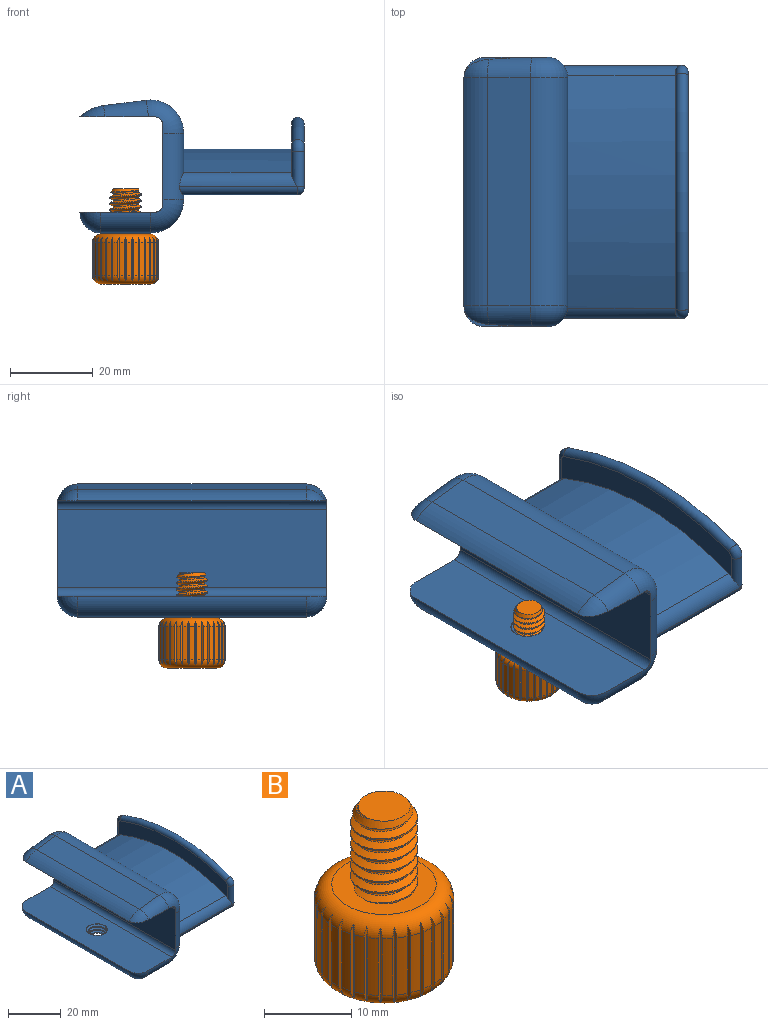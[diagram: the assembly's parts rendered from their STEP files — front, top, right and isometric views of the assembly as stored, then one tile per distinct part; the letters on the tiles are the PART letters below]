
ASSEMBLY  parts=2 mates=1
PART A: 48 faces, bbox 55x65.4x35.4 mm
  f0: plane 55x12mm, normal (0,0,-1), area 596.4mm2, adj f11,f21,f27,f45,f47
  f1: plane 55x7.37mm, normal (1,0,0), area 299.3mm2, adj f11,f12,f19,f25
  f2: cylinder r=71.97mm len=56.12mm, axis (-1,0,0), area 1498.9mm2, adj f3,f14,f19,f25,f28,f29
  f3: plane 55x9.15mm, normal (1,0,0), area 301.4mm2, adj f2,f4,f19,f25
  f4: cylinder r=8mm len=55mm, axis (0,1,0), area 745.8mm2, adj f3,f5,f18,f24
  f5: plane 55x10.32mm, normal (-0.12,0,0.99), area 572.1mm2, adj f4,f15,f17,f23
  f6: plane 65.07x18.25mm, normal (0,0,-1), area 1145.5mm2, adj f7,f15,f16,f17,f18,f22,f23,f24
  f7: cylinder r=2mm len=64.93mm, axis (0,1,0), area 203.7mm2, adj f6,f8,f18,f24
  f8: plane 65.32x19.32mm, normal (-1,0,0), area 1235mm2, adj f7,f9,f18,f19,f20,f24,f25,f26
  f9: cylinder r=2mm len=64.99mm, axis (0,1,0), area 204.2mm2, adj f8,f10,f20,f26
  f10: plane 65.43x18.43mm, normal (0,0,1), area 1112.2mm2, adj f9,f20,f21,f26,f27,f40,f41,f42
  f11: cylinder r=8mm len=55mm, axis (0,1,0), area 691.2mm2, adj f0,f1,f20,f26
  f12: cylinder r=66.97mm len=55.35mm, axis (-1,0,0), area 1569.1mm2, adj f1,f19,f25,f30,f31,f39
  f13: plane 58x15.66mm, normal (1,0,0), area 565.9mm2, adj f32,f33,f34,f35,f36,f37,f38,f39
  f14: plane 58x12.26mm, normal (-1,0,0), area 357.1mm2, adj f2,f28,f29,f32,f33,f34,f35,f36
  f15: cylinder r=10mm len=55mm, axis (0,-1,0), area 352.5mm2, adj f5,f6,f16,f22
  f16: torus R=5mm, axis (0,-1,0), area 25.3mm2, adj f6,f15,f17
  f17: cylinder r=5mm len=10.82mm, axis (-0.99,0,-0.12), area 64.4mm2, adj f5,f6,f16,f18
  f18: torus R=3mm, axis (0,-1,0), area 77.8mm2, adj f4,f6,f7,f8,f17,f19
  f19: cylinder r=5mm len=16.06mm, axis (0,0,1), area 112.4mm2, adj f1,f2,f3,f8,f12,f18,f20,f29
  f20: torus R=3mm, axis (0,-1,0), area 75.2mm2, adj f8,f9,f10,f11,f19,f21
  f21: cylinder r=5mm len=12mm, axis (1,0,0), area 94.2mm2, adj f0,f10,f20,f44
  f22: torus R=5mm, axis (0,-1,0), area 25.3mm2, adj f6,f15,f23
  f23: cylinder r=5mm len=10.82mm, axis (0.99,0,0.12), area 64.4mm2, adj f5,f6,f22,f24
  f24: torus R=3mm, axis (0,-1,0), area 77.8mm2, adj f4,f6,f7,f8,f23,f25
  f25: cylinder r=5mm len=16.06mm, axis (0,0,-1), area 112.4mm2, adj f1,f2,f3,f8,f12,f24,f26,f28
  f26: torus R=3mm, axis (0,-1,0), area 75.2mm2, adj f8,f9,f10,f11,f25,f27
  f27: cylinder r=5mm len=12mm, axis (-1,0,0), area 94.2mm2, adj f0,f10,f26,f46
  f28: cylinder r=4mm len=28.5mm, axis (-1,0,0), area 122.8mm2, adj f2,f14,f25,f30,f36,f38
  f29: cylinder r=4mm len=28.5mm, axis (-1,0,0), area 122.8mm2, adj f2,f14,f19,f31,f35,f37
  f30: cylinder r=2mm len=28.5mm, axis (-1,0,0), area 109.3mm2, adj f12,f25,f28,f38
  f31: cylinder r=2mm len=28.5mm, axis (-1,0,0), area 109.3mm2, adj f12,f19,f29,f37
  f32: torus R=77.97mm, axis (1,0,0), area 273.6mm2, adj f13,f14,f33,f34
  f33: torus R=1.5mm, axis (1,0,0), area 13.9mm2, adj f13,f14,f32,f35
  f34: torus R=1.5mm, axis (1,0,0), area 13.9mm2, adj f13,f14,f32,f36
  f35: cylinder r=1.5mm len=8.55mm, axis (0,0,-1), area 37mm2, adj f13,f14,f29,f33,f37
  f36: cylinder r=1.5mm len=8.55mm, axis (0,0,1), area 37mm2, adj f13,f14,f28,f34,f38
  f37: torus R=0.5mm, axis (1,0,0), area 6.9mm2, adj f13,f29,f31,f35,f39
  f38: torus R=0.5mm, axis (1,0,0), area 6.9mm2, adj f13,f28,f30,f36,f39
  f39: torus R=68.47mm, axis (1,0,0), area 135.5mm2, adj f12,f13,f37,f38
  f40: bspline ~9.96x8.62mm, area 67.9mm2, adj f10,f42,f43,f47
  f41: bspline ~9.96x8.62mm, area 68mm2, adj f10,f42,f43,f47
  f42: bspline ~10.12x8.76mm, area 19mm2, adj f10,f40,f41,f47
  f43: cylinder r=3.5mm len=7mm, axis (0,0,1), area 22mm2, adj f10,f40,f41,f47
  f44: sphere r=5mm, area 39.3mm2, adj f10,f21,f45
  f45: cylinder r=5mm len=55mm, axis (0,-1,0), area 432mm2, adj f0,f10,f44,f46
  f46: sphere r=5mm, area 39.3mm2, adj f10,f27,f45
  f47: cone r=4.5mm half-angle=45deg, axis (0,0,-1), area 23.4mm2, adj f0,f40,f41,f42,f43
PART B: 100 faces, bbox 17.7x17.7x23.9 mm
  f0: cylinder r=3.85mm len=9.53mm, axis (0,0,1), area 21.6mm2, adj f2,f3,f37,f99
  f1: bspline ~12.13x7.02mm, area 57.8mm2, adj f2,f3,f37,f38,f99
  f2: bspline ~11.72x8.89mm, area 138.5mm2, adj f0,f1,f37,f99
  f3: bspline ~12.22x8.89mm, area 138.1mm2, adj f0,f1,f37,f99
  f4: cylinder r=8mm len=8mm, axis (0,0,1), area 9.7mm2, adj f33,f34,f96,f97
  f5: cylinder r=8mm len=8mm, axis (0,0,1), area 9.7mm2, adj f33,f34,f94,f95
  f6: cylinder r=8mm len=8mm, axis (0,0,1), area 9.7mm2, adj f33,f34,f92,f93
  f7: cylinder r=8mm len=8mm, axis (0,0,1), area 9.7mm2, adj f33,f34,f90,f91
  f8: cylinder r=8mm len=8mm, axis (0,0,1), area 9.7mm2, adj f33,f34,f88,f89
  f9: cylinder r=8mm len=8mm, axis (0,0,1), area 9.7mm2, adj f33,f34,f86,f87
  f10: cylinder r=8mm len=8mm, axis (0,0,1), area 9.7mm2, adj f33,f34,f84,f85
  f11: cylinder r=8mm len=8mm, axis (0,0,1), area 9.7mm2, adj f33,f34,f82,f83
  f12: cylinder r=8mm len=8mm, axis (0,0,1), area 9.7mm2, adj f33,f34,f80,f81
  f13: cylinder r=8mm len=8mm, axis (0,0,1), area 9.7mm2, adj f33,f34,f78,f79
  f14: cylinder r=8mm len=8mm, axis (0,0,1), area 9.7mm2, adj f33,f34,f76,f77
  f15: cylinder r=8mm len=8mm, axis (0,0,1), area 9.7mm2, adj f33,f34,f74,f75
  f16: cylinder r=8mm len=8mm, axis (0,0,1), area 9.7mm2, adj f33,f34,f72,f73
  f17: cylinder r=8mm len=8mm, axis (0,0,1), area 9.7mm2, adj f33,f34,f70,f71
  f18: cylinder r=8mm len=8mm, axis (0,0,1), area 9.7mm2, adj f33,f34,f68,f69
  f19: cylinder r=8mm len=8mm, axis (0,0,1), area 9.7mm2, adj f33,f34,f66,f67
  f20: cylinder r=8mm len=8mm, axis (0,0,1), area 9.7mm2, adj f33,f34,f64,f65
  f21: cylinder r=8mm len=8mm, axis (0,0,1), area 9.7mm2, adj f33,f34,f62,f63
  f22: cylinder r=8mm len=8mm, axis (0,0,1), area 9.7mm2, adj f33,f34,f60,f61
  f23: cylinder r=8mm len=8mm, axis (0,0,1), area 9.7mm2, adj f33,f34,f58,f59
  f24: cylinder r=8mm len=8mm, axis (0,0,1), area 9.7mm2, adj f33,f34,f56,f57
  f25: cylinder r=8mm len=8mm, axis (0,0,1), area 9.7mm2, adj f33,f34,f54,f55
  f26: cylinder r=8mm len=8mm, axis (0,0,1), area 9.7mm2, adj f33,f34,f52,f53
  f27: cylinder r=8mm len=8mm, axis (0,0,1), area 9.7mm2, adj f33,f34,f50,f51
  f28: cylinder r=8mm len=8mm, axis (0,0,1), area 9.7mm2, adj f33,f34,f48,f49
  f29: cylinder r=8mm len=8mm, axis (0,0,1), area 9.7mm2, adj f33,f34,f46,f47
  f30: cylinder r=8mm len=8mm, axis (0,0,1), area 9.7mm2, adj f33,f34,f44,f45
  f31: cylinder r=8mm len=8mm, axis (0,0,1), area 9.7mm2, adj f33,f34,f42,f43
  f32: cylinder r=8mm len=8mm, axis (0,0,1), area 9.7mm2, adj f33,f34,f40,f41
  f33: torus R=6mm, axis (0,0,1), area 134.8mm2, adj f4,f5,f6,f7,f8,f9,f10,f11
  f34: torus R=6mm, axis (0,0,-1), area 134.8mm2, adj f4,f5,f6,f7,f8,f9,f10,f11
  f35: plane 12x12mm, normal (0,0,-1), area 113.1mm2, adj f33
  f36: cylinder r=8mm len=8mm, axis (0,0,1), area 9.7mm2, adj f33,f34,f39,f98
  f37: plane 12.41x12.41mm, normal (0,0,1), area 76.9mm2, adj f0,f1,f2,f3,f34
  f38: plane 6.05x6.02mm, normal (0,0,1), area 28.2mm2, adj f1,f99
  f39: plane 10.51x0.51mm, normal (0.87,-0.5,0), area 4.4mm2, adj f33,f34,f36,f40
  f40: plane 10.51x0.51mm, normal (-0.87,-0.5,0), area 4.4mm2, adj f32,f33,f34,f39
  f41: plane 10.51x0.55mm, normal (0.95,-0.31,0), area 4.4mm2, adj f32,f33,f34,f42
  f42: plane 10.51x0.45mm, normal (-0.74,-0.67,0), area 4.4mm2, adj f31,f33,f34,f41
  f43: plane 10.51x0.57mm, normal (0.99,-0.1,0), area 4.4mm2, adj f31,f33,f34,f44
  f44: plane 10.51x0.48mm, normal (-0.59,-0.81,0), area 4.4mm2, adj f30,f33,f34,f43
  f45: plane 10.51x0.57mm, normal (0.99,0.1,0), area 4.4mm2, adj f30,f33,f34,f46
  f46: plane 10.51x0.53mm, normal (-0.41,-0.91,0), area 4.4mm2, adj f29,f33,f34,f45
  f47: plane 10.51x0.55mm, normal (0.95,0.31,0), area 4.4mm2, adj f29,f33,f34,f48
  f48: plane 10.51x0.56mm, normal (-0.21,-0.98,0), area 4.4mm2, adj f28,f33,f34,f47
  f49: plane 10.51x0.51mm, normal (0.87,0.5,0), area 4.4mm2, adj f28,f33,f34,f50
  f50: plane 10.52x0.57mm, normal (0,-1,0), area 4.4mm2, adj f27,f33,f34,f49
  f51: plane 10.51x0.45mm, normal (0.74,0.67,0), area 4.4mm2, adj f27,f33,f34,f52
  f52: plane 10.51x0.56mm, normal (0.21,-0.98,0), area 4.4mm2, adj f26,f33,f34,f51
  f53: plane 10.51x0.48mm, normal (0.59,0.81,0), area 4.4mm2, adj f26,f33,f34,f54
  f54: plane 10.51x0.53mm, normal (0.41,-0.91,0), area 4.4mm2, adj f25,f33,f34,f53
  f55: plane 10.51x0.53mm, normal (0.41,0.91,0), area 4.4mm2, adj f25,f33,f34,f56
  f56: plane 10.51x0.48mm, normal (0.59,-0.81,0), area 4.4mm2, adj f24,f33,f34,f55
  f57: plane 10.51x0.56mm, normal (0.21,0.98,0), area 4.4mm2, adj f24,f33,f34,f58
  f58: plane 10.51x0.45mm, normal (0.74,-0.67,0), area 4.4mm2, adj f23,f33,f34,f57
  f59: plane 10.52x0.57mm, normal (0,1,0), area 4.4mm2, adj f23,f33,f34,f60
  f60: plane 10.51x0.51mm, normal (0.87,-0.5,0), area 4.4mm2, adj f22,f33,f34,f59
  f61: plane 10.51x0.56mm, normal (-0.21,0.98,0), area 4.4mm2, adj f22,f33,f34,f62
  f62: plane 10.51x0.55mm, normal (0.95,-0.31,0), area 4.4mm2, adj f21,f33,f34,f61
  f63: plane 10.51x0.53mm, normal (-0.41,0.91,0), area 4.4mm2, adj f21,f33,f34,f64
  f64: plane 10.51x0.57mm, normal (0.99,-0.1,0), area 4.4mm2, adj f20,f33,f34,f63
  f65: plane 10.51x0.48mm, normal (-0.59,0.81,0), area 4.4mm2, adj f20,f33,f34,f66
  f66: plane 10.51x0.57mm, normal (0.99,0.1,0), area 4.4mm2, adj f19,f33,f34,f65
  f67: plane 10.51x0.45mm, normal (-0.74,0.67,0), area 4.4mm2, adj f19,f33,f34,f68
  f68: plane 10.51x0.55mm, normal (0.95,0.31,0), area 4.4mm2, adj f18,f33,f34,f67
  f69: plane 10.51x0.51mm, normal (-0.87,0.5,0), area 4.4mm2, adj f18,f33,f34,f70
  f70: plane 10.51x0.51mm, normal (0.87,0.5,0), area 4.4mm2, adj f17,f33,f34,f69
  f71: plane 10.51x0.55mm, normal (-0.95,0.31,0), area 4.4mm2, adj f17,f33,f34,f72
  f72: plane 10.51x0.45mm, normal (0.74,0.67,0), area 4.4mm2, adj f16,f33,f34,f71
  f73: plane 10.51x0.57mm, normal (-0.99,0.1,0), area 4.4mm2, adj f16,f33,f34,f74
  f74: plane 10.51x0.48mm, normal (0.59,0.81,0), area 4.4mm2, adj f15,f33,f34,f73
  f75: plane 10.51x0.57mm, normal (-0.99,-0.1,0), area 4.4mm2, adj f15,f33,f34,f76
  f76: plane 10.51x0.53mm, normal (0.41,0.91,0), area 4.4mm2, adj f14,f33,f34,f75
  f77: plane 10.51x0.55mm, normal (-0.95,-0.31,0), area 4.4mm2, adj f14,f33,f34,f78
  f78: plane 10.51x0.56mm, normal (0.21,0.98,0), area 4.4mm2, adj f13,f33,f34,f77
  f79: plane 10.51x0.51mm, normal (-0.87,-0.5,0), area 4.4mm2, adj f13,f33,f34,f80
  f80: plane 10.52x0.57mm, normal (0,1,0), area 4.4mm2, adj f12,f33,f34,f79
  f81: plane 10.51x0.45mm, normal (-0.74,-0.67,0), area 4.4mm2, adj f12,f33,f34,f82
  f82: plane 10.51x0.56mm, normal (-0.21,0.98,0), area 4.4mm2, adj f11,f33,f34,f81
  f83: plane 10.51x0.48mm, normal (-0.59,-0.81,0), area 4.4mm2, adj f11,f33,f34,f84
  f84: plane 10.51x0.53mm, normal (-0.41,0.91,0), area 4.4mm2, adj f10,f33,f34,f83
  f85: plane 10.51x0.53mm, normal (-0.41,-0.91,0), area 4.4mm2, adj f10,f33,f34,f86
  f86: plane 10.51x0.48mm, normal (-0.59,0.81,0), area 4.4mm2, adj f9,f33,f34,f85
  f87: plane 10.51x0.56mm, normal (-0.21,-0.98,0), area 4.4mm2, adj f9,f33,f34,f88
  f88: plane 10.51x0.45mm, normal (-0.74,0.67,0), area 4.4mm2, adj f8,f33,f34,f87
  f89: plane 10.52x0.57mm, normal (0,-1,0), area 4.4mm2, adj f8,f33,f34,f90
  f90: plane 10.51x0.51mm, normal (-0.87,0.5,0), area 4.4mm2, adj f7,f33,f34,f89
  f91: plane 10.51x0.56mm, normal (0.21,-0.98,0), area 4.4mm2, adj f7,f33,f34,f92
  f92: plane 10.51x0.55mm, normal (-0.95,0.31,0), area 4.4mm2, adj f6,f33,f34,f91
  f93: plane 10.51x0.53mm, normal (0.41,-0.91,0), area 4.4mm2, adj f6,f33,f34,f94
  f94: plane 10.51x0.57mm, normal (-0.99,0.1,0), area 4.4mm2, adj f5,f33,f34,f93
  f95: plane 10.51x0.48mm, normal (0.59,-0.81,0), area 4.4mm2, adj f5,f33,f34,f96
  f96: plane 10.51x0.57mm, normal (-0.99,-0.1,0), area 4.4mm2, adj f4,f33,f34,f95
  f97: plane 10.51x0.45mm, normal (0.74,-0.67,0), area 4.4mm2, adj f4,f33,f34,f98
  f98: plane 10.51x0.55mm, normal (-0.95,-0.31,0), area 4.4mm2, adj f33,f34,f36,f97
  f99: cone r=3mm half-angle=30deg, axis (0,0,-1), area 16.1mm2, adj f0,f1,f2,f3,f38
PLACE A at identity fixed
PLACE B t=(-9,0,-40.29)mm
MATE slider B.f0 <-> A.f47  axis (0,0,1) through (-9,0,-34.29)mm
